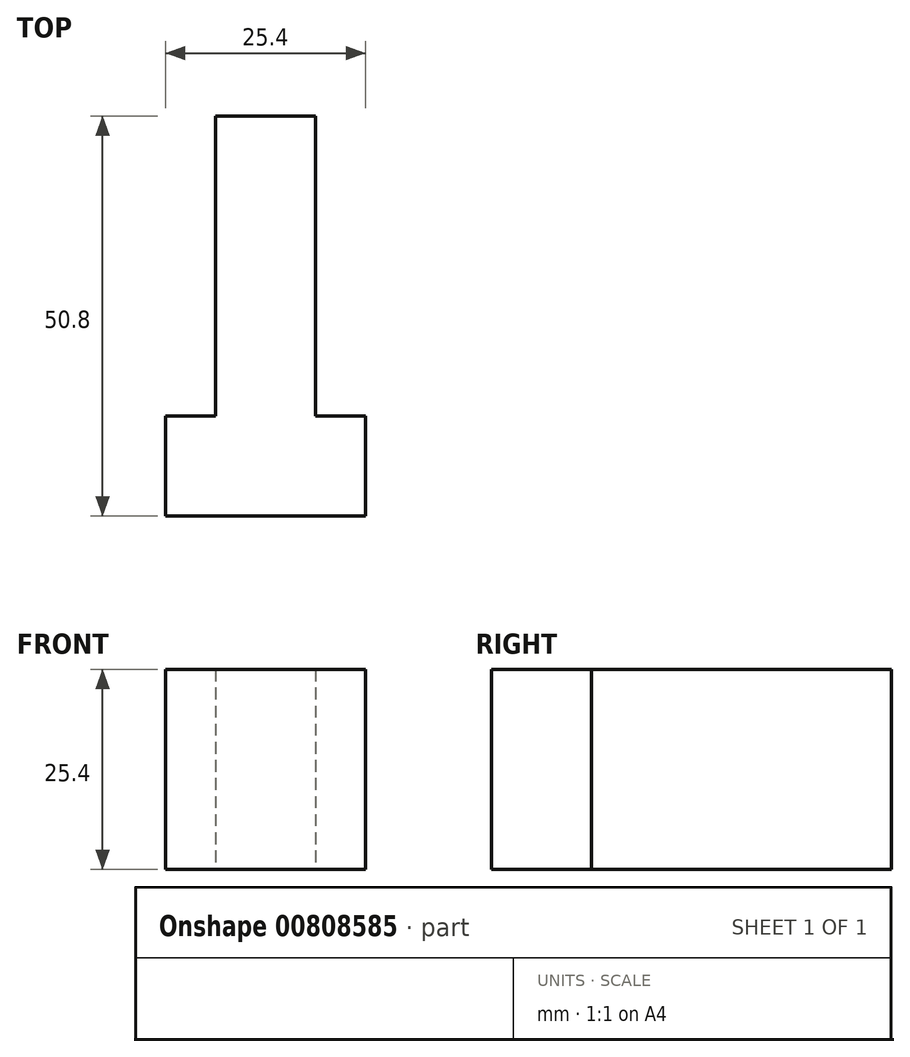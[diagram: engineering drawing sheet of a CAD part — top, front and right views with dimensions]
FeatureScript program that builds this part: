
annotation { "Feature Type Name" : "Feature", "Feature Type Description" : "" }
export const myFeature = defineFeature(function(context is Context, id is Id, definition is map)
    precondition{}
    {
        {
            var Q0;
            Q0=qCreatedBy(makeId("Top.planeOp"),FACE);
            var sketch = newSketch(context, id + "F0", { "sketchPlane" : qUnion([Q0])});
            skLineSegment(sketch, "E0", {"start": v(0, 0) * mm, "end": v(25.4, 0) * mm});
            skLineSegment(sketch, "E1", {"start": v(25.4, 0) * mm, "end": v(25.4, 12.7) * mm});
            skLineSegment(sketch, "E2", {"start": v(25.4, 12.7) * mm, "end": v(19.05, 12.7) * mm});
            skLineSegment(sketch, "E3", {"start": v(19.05, 12.7) * mm, "end": v(19.05, 50.8) * mm});
            skLineSegment(sketch, "E4", {"start": v(19.05, 50.8) * mm, "end": v(6.35, 50.8) * mm});
            skLineSegment(sketch, "E5", {"start": v(6.35, 50.8) * mm, "end": v(6.35, 12.7) * mm});
            skLineSegment(sketch, "E6", {"start": v(6.35, 12.7) * mm, "end": v(0, 12.7) * mm});
            skLineSegment(sketch, "E7", {"start": v(0, 12.7) * mm, "end": v(0, 0) * mm});
            skSolve(sketch);
        }
        {
            var Q0;
            Q0 = qSketchRegion(id + "F0", true);
            extrude(context, id + "F1", {"entities" : qUnion([Q0]), "depth" : 25.4 * mm, "offsetDistance" : 25.4 * mm});
        }
    });
